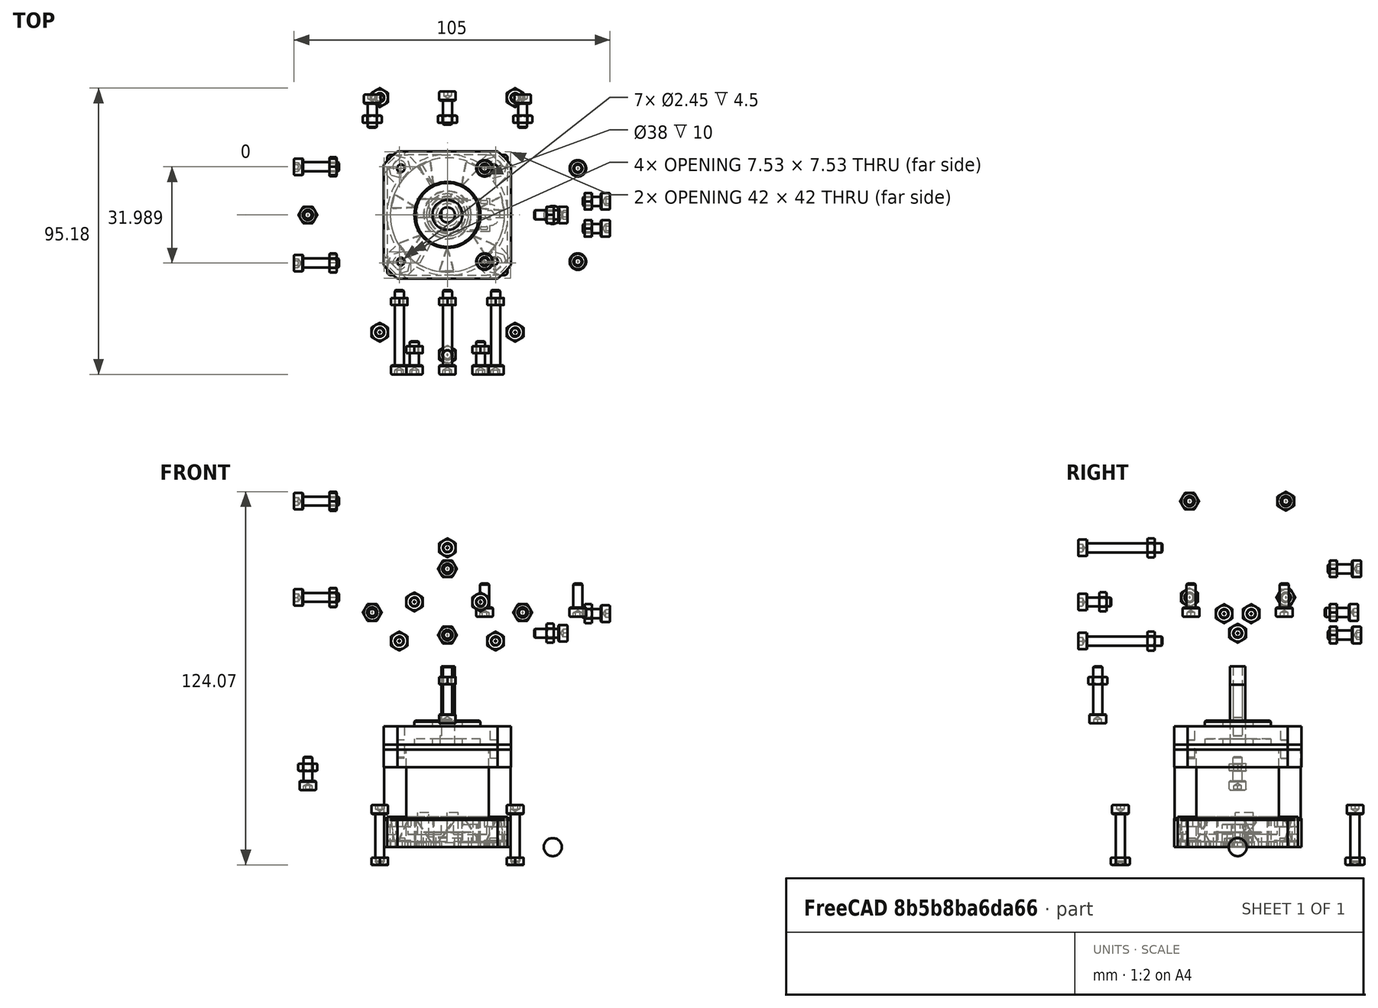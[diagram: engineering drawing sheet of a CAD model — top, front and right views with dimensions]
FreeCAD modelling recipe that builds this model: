
FCSTD DOCUMENT  (FreeCAD 0.19R24276 (Git))
Label: AssemblyArt3
License: All rights reserved
LicenseURL: http://en.wikipedia.org/wiki/All_rights_reserved
objects: Part::FeaturePython×49, App::Link×14, PartDesign::CoordinateSystem×13, App::Part×7, App::DocumentObjectGroup×6, Part::Feature×5, PartDesign::Line×5, App::FeaturePython×1, Part::Sphere×1
note: 72 computed B-rep shape members (.brp) not serialized (recipe doc carries the construction recipe, not evaluated geometry)
EXTERNAL_REF file=Art3Body.FCStd obj=LCS_Bottom
EXTERNAL_REF file=Art3Body.FCStd obj=Body002
EXTERNAL_REF file=Art23Optodisk.FCStd obj=LCS_Art23Optodisk
EXTERNAL_REF file=Art3Body.FCStd obj=LCS_OptoDisk
EXTERNAL_REF file=Art23Optodisk.FCStd obj=Body
EXTERNAL_REF file=Art3Body.FCStd obj=LCS_Pulley
EXTERNAL_REF file=Art3Pulley.FCStd obj=LCS_Art3Pulley
EXTERNAL_REF file=Art3Pulley.FCStd obj=Body
EXTERNAL_REF file=Art3Body.FCStd obj=LCS_Art4MotorHolder
EXTERNAL_REF file=Art4MotorFix.FCStd obj=LCS_Art4MotorFix
EXTERNAL_REF file=Art4MotorFix.FCStd obj=Body
EXTERNAL_REF file=Art4MotorFix.FCStd obj=LCS_Art4Motor
EXTERNAL_REF file=Art4MotorGear.FCStd obj=LCS_Art4MotorGear
EXTERNAL_REF file=Art4MotorGear.FCStd obj=Body
EXTERNAL_REF file=Art3Body.FCStd obj=LCS_Fan
EXTERNAL_REF file=Art3Body.FCStd obj=LCS_Bearing
EXTERNAL_REF file=Art3Pulley.FCStd obj=LCS_Bearing
EXTERNAL_REF file=Art3Pulley.FCStd obj=LCS_BearingFix
EXTERNAL_REF file=CommonBearingFixThrough.FCStd obj=LCS_CommonBearingFixThrough
EXTERNAL_REF file=CommonBearingFixThrough.FCStd obj=Body
EXTERNAL_REF file=Art3Body.FCStd obj=LCS_BearingFix
EXTERNAL_REF file=Art3Body.FCStd obj=LCS_OptoSensor
EXTERNAL_REF file=Art4BearingRing.FCStd obj=LCS_Art4BearingRing
EXTERNAL_REF file=Art4BearingRing.FCStd obj=Body
EXTERNAL_REF file=Art4BearingRing.FCStd obj=LCS_BallBearings
EXTERNAL_REF file=Art3Body.FCStd obj=HoleAxis_8
EXTERNAL_REF file=Art3Body.FCStd obj=HoleAxis_9
EXTERNAL_REF file=Art3Body.FCStd obj=HoleAxis_7
EXTERNAL_REF file=Art3Body.FCStd obj=HoleAxis_14
EXTERNAL_REF file=Art3Body.FCStd obj=HoleAxis_11
EXTERNAL_REF file=Art3Body.FCStd obj=HoleAxis_10
EXTERNAL_REF file=Art3Body.FCStd obj=HoleAxis_12
EXTERNAL_REF file=Art3Body.FCStd obj=HoleAxis_13
EXTERNAL_REF file=Art3Pulley.FCStd obj=HoleAxis_6
EXTERNAL_REF file=Art3Pulley.FCStd obj=HoleAxis_5
EXTERNAL_REF file=Art3Pulley.FCStd obj=HoleAxis_3
EXTERNAL_REF file=Art4MotorFix.FCStd obj=HoleAxis_2
EXTERNAL_REF file=Art4MotorFix.FCStd obj=HoleAxis_3
EXTERNAL_REF file=Art4MotorGear.FCStd obj=HoleAxis_2
EXTERNAL_REF file=Art4BearingRing.FCStd obj=HoleAxis_4
EXTERNAL_REF file=Art4BearingRing.FCStd obj=HoleAxis_3
EXTERNAL_REF file=Art4BearingRing.FCStd obj=HoleAxis_1
EXTERNAL_REF file=Art4BearingRing.FCStd obj=HoleAxis_2
EXTERNAL_REF file=CommonBearingFixThrough.FCStd obj=HoleAxis_1
EXTERNAL_REF file=CommonBearingFixThrough.FCStd obj=HoleAxis_2
EXTERNAL_REF file=Art23Optodisk.FCStd obj=HoleAxis_1
EXTERNAL_REF file=Art23Optodisk.FCStd obj=HoleAxis_2
EXTERNAL_REF file=Art3Pulley.FCStd obj=HoleAxis_1
EXTERNAL_REF file=Art3Pulley.FCStd obj=HoleAxis_4
EXTERNAL_REF file=Art3Pulley.FCStd obj=HoleAxis_2
EXTERNAL_REF file=Art3Body.FCStd obj=HoleAxis_2
EXTERNAL_REF file=Art3Body.FCStd obj=HoleAxis_1
EXTERNAL_REF file=Art3Body.FCStd obj=HoleAxis_4
EXTERNAL_REF file=Art3Body.FCStd obj=HoleAxis_3
EXTERNAL_REF file=Art3Body.FCStd obj=HoleAxis_18
EXTERNAL_REF file=Art3Body.FCStd obj=HoleAxis_17
EXTERNAL_REF file=Art3Body.FCStd obj=HoleAxis_16
EXTERNAL_REF file=Art3Body.FCStd obj=HoleAxis_15
EXTERNAL_REF file=Art4MotorFix.FCStd obj=HoleAxis_5
EXTERNAL_REF file=Art4MotorFix.FCStd obj=HoleAxis_6
EXTERNAL_REF file=Art4MotorFix.FCStd obj=HoleAxis_4
EXTERNAL_REF file=Art4MotorFix.FCStd obj=HoleAxis_1
EXTERNAL_REF file=Art3Body.FCStd obj=HoleAxis_6
EXTERNAL_REF file=Art3Body.FCStd obj=HoleAxis_5
EXTERNAL_REF file=Art4MotorGear.FCStd obj=HoleAxis_1

FEATURE [PartDesign::CoordinateSystem] LCS_Origin
  AttacherType = Attacher::AttachEngine3D
  MapMode = 2
  Support = -> [X_Axis]
FEATURE [App::DocumentObjectGroup] Constraints
FEATURE [App::FeaturePython] Variables  # WARN: FeaturePython — macro-defined, semantics opaque (R4)
FEATURE [App::Link] Art3Body_Art3Body
  AssemblyType = Asm4EE
  AttachedBy = #LCS_Art3Body
  AttachedTo = Parent Assembly#LCS_Origin
  ElementCount = 0
  LinkPlacement = pos=(-6.7e-15,2.7e-15,-7) rot=(0,0,1;0rad)
  LinkTransform = false
  Placement = pos=(-6.7e-15,2.7e-15,-7) rot=(0,0,1;0rad)
  Scale = 1
  ScaleVector = (1,1,1)
  ShowElement = true
  expr: Placement = LCS_Origin.Placement * AttachmentOffset * Art3Body#<<LCS_Art3Body>>.Placement ^ -1
FEATURE [App::Link] Art23Optodisk_Art23Optodisk
  AssemblyType = Asm4EE
  AttachedBy = #LCS_Art23Optodisk
  AttachedTo = Art3Body_Art3Body#LCS_OptoRing
  AttachmentOffset = pos=(0,0,0) rot=(0,0,1;3.14159rad)
  ElementCount = 0
  LinkPlacement = pos=(-3.27e-14,35,81.5) rot=(1,0,0;4.71239rad)
  LinkTransform = false
  Placement = pos=(-3.27e-14,35,81.5) rot=(1,0,0;4.71239rad)
  Scale = 1
  ScaleVector = (1,1,1)
  ShowElement = true
  expr: Placement = Art3Body_Art3Body.Placement * Art3Body#<<LCS_OptoRing>>.Placement * AttachmentOffset * Art23Optodisk#LCS_Art23Optodisk.Placement ^ -1
FEATURE [App::Link] Art3Pulley_Art3Pulley
  AssemblyType = Asm4EE
  AttachedBy = #LCS_Art3Pulley
  AttachedTo = Art3Body_Art3Body#LCS_Pulley
  ElementCount = 0
  LinkPlacement = pos=(-2.65e-14,-53,81.5) rot=(-1,0,0;1.5708rad)
  LinkTransform = false
  Placement = pos=(-2.65e-14,-53,81.5) rot=(-1,0,0;1.5708rad)
  Scale = 1
  ScaleVector = (1,1,1)
  ShowElement = true
  expr: Placement = Art3Body_Art3Body.Placement * Art3Body#LCS_Pulley.Placement * AttachmentOffset * Art3Pulley#LCS_Art3Pulley.Placement ^ -1
FEATURE [App::Link] Art4MotorFix_Art4MotorFix
  AssemblyType = Asm4EE
  AttachedBy = #LCS_Art4MotorFix
  AttachedTo = Art3Body_Art3Body#LCS_MotorHolder
  AttachmentOffset = pos=(0,0,0) rot=(0,-1,0;3.14159rad)
  ElementCount = 0
  LinkPlacement = pos=(27.85,-1.36e-14,82.6) rot=(0,1,0;3.14159rad)
  LinkTransform = false
  Placement = pos=(27.85,-1.36e-14,82.6) rot=(0,1,0;3.14159rad)
  Scale = 1
  ScaleVector = (1,1,1)
  ShowElement = true
  expr: Placement = Art3Body_Art3Body.Placement * Art3Body#<<LCS_MotorHolder>>.Placement * AttachmentOffset * Art4MotorFix#LCS_Art4MotorFix.Placement ^ -1
FEATURE [PartDesign::CoordinateSystem] LCS_0008
  AttacherType = Attacher::AttachEngine3D
  MapMode = 2
  Support = -> [X_Axis009]
FEATURE [Part::Feature] Part__Feature031  label="Nema-17-motor-40mm-final"
FEATURE [PartDesign::CoordinateSystem] LCS_Stepper_Nema17x40
  AttacherType = Attacher::AttachEngine3D
  MapMode = 45
  Placement = pos=(7.5e-15,0,0) rot=(0,0,1;0rad)
  Support = -> [Part__Feature031]
FEATURE [PartDesign::CoordinateSystem] LCS_Gear2  label="LCS_Gear"
  AttacherType = Attacher::AttachEngine3D
  AttachmentOffset = pos=(0,0,1.9) rot=(0,0,1;0rad)
  MapMode = 11
  Placement = pos=(0,0,44) rot=(0,0,1;1.5708rad)
  Support = -> [Part__Feature031]
FEATURE [App::Part] Stepper_Nema17x40
  Group = -> [LCS_0008,Part__Feature031,LCS_Stepper_Nema17x40,LCS_Gear2]
  Origin = -> Origin009
FEATURE [Part::Feature] Cut001
FEATURE [PartDesign::CoordinateSystem] LCS_OpticSensor
  AttacherType = Attacher::AttachEngine3D
  MapMode = 11
  Placement = pos=(14,0,0) rot=(0,0,1;1.5708rad)
  Support = -> [Cut001]
FEATURE [PartDesign::Line] HoleAxis_1
  AttacherType = Attacher::AttachEngineLine
  Length = 4.2272
  MapMode = 19
  Placement = pos=(14,0,1.5) rot=(0,0,1;0rad)
  ResizeMode = 1
  Support = -> [Cut001]
FEATURE [App::Part] Part  label="OpticSensor"
  Group = -> [Cut001,LCS_OpticSensor,HoleAxis_1]
  Origin = -> Origin010
FEATURE [Part::Feature] Chamfer_solid  label="NEMA-17_Stepper_Motor_34mm"
FEATURE [PartDesign::CoordinateSystem] LCS_Stepper_Nema17x34
  AttacherType = Attacher::AttachEngine3D
  MapMode = 45
  Placement = pos=(7.4e-15,0,34) rot=(0,0,1;0rad)
  Support = -> [Chamfer_solid]
FEATURE [PartDesign::CoordinateSystem] LCS_Gear  label="LCS_Gear001"
  AttacherType = Attacher::AttachEngine3D
  AttachmentOffset = pos=(0,0,4) rot=(0,0,1;0rad)
  MapMode = 11
  Placement = pos=(0,0,40) rot=(0,0,1;1.5708rad)
  Support = -> [Chamfer_solid]
FEATURE [App::Part] Stepper_Nema17x34
  Group = -> [Chamfer_solid,LCS_Stepper_Nema17x34,LCS_Gear]
  Origin = -> Origin011
FEATURE [App::DocumentObjectGroup] Group  label="Electronics"
  Group = -> [Stepper_Nema17x40,Part,Stepper_Nema17x34]
FEATURE [App::Link] Stepper_Nema17x34001
  AssemblyType = Asm4EE
  AttachedBy = #LCS_Stepper_Nema17x34
  AttachedTo = Art4MotorFix_Art4MotorFix#LCS_Art4Motor
  ElementCount = 0
  LinkPlacement = pos=(27.85,-1.179e-13,116.6) rot=(0,1,0;3.14159rad)
  LinkTransform = false
  Placement = pos=(27.85,-1.179e-13,116.6) rot=(0,1,0;3.14159rad)
  Scale = 1
  ScaleVector = (1,1,1)
  ShowElement = true
  expr: Placement = Art4MotorFix_Art4MotorFix.Placement * Art4MotorFix#LCS_Art4Motor.Placement * AttachmentOffset * LCS_Stepper_Nema17x34.Placement ^ -1
FEATURE [App::Link] Art4MotorGear_Art4MotorGear
  AssemblyType = Asm4EE
  AttachedBy = #LCS_Art4MotorGear
  AttachedTo = Stepper_Nema17x34001#LCS_Gear
  AttachmentOffset = pos=(0,0,0) rot=(0,1,0;3.14159rad)
  ElementCount = 0
  LinkPlacement = pos=(27.85,3.49e-14,66.6) rot=(0,-1,0;3.14159rad)
  LinkTransform = false
  Placement = pos=(27.85,3.49e-14,66.6) rot=(0,-1,0;3.14159rad)
  Scale = 1
  ScaleVector = (1,1,1)
  ShowElement = true
  expr: Placement = Stepper_Nema17x34001.Placement * LCS_Gear.Placement * AttachmentOffset * Art4MotorGear#LCS_Art4MotorGear.Placement ^ -1
FEATURE [Part::Feature] Part__Feature001  label="fan-40x40mm"
FEATURE [PartDesign::Line] HoleAxis_8
  AttacherType = Attacher::AttachEngineLine
  Length = 6.05899
  MapMode = 19
  Placement = pos=(-15.9948,15.9948,6.76) rot=(0,0,1;0rad)
  ResizeMode = 1
  Support = -> [Part__Feature001]
FEATURE [PartDesign::Line] HoleAxis_5
  AttacherType = Attacher::AttachEngineLine
  Length = 6.05899
  MapMode = 19
  Placement = pos=(15.9948,15.9948,6.76) rot=(0,0,1;4.71239rad)
  ResizeMode = 1
  Support = -> [Part__Feature001]
FEATURE [PartDesign::Line] HoleAxis_7
  AttacherType = Attacher::AttachEngineLine
  Length = 6.05899
  MapMode = 19
  Placement = pos=(-15.9948,-15.9948,6.76) rot=(0,0,1;1.5708rad)
  ResizeMode = 1
  Support = -> [Part__Feature001]
FEATURE [PartDesign::Line] HoleAxis_6
  AttacherType = Attacher::AttachEngineLine
  Length = 6.05899
  MapMode = 19
  Placement = pos=(15.9948,-15.9948,6.76) rot=(0,0,1;3.14159rad)
  ResizeMode = 1
  Support = -> [Part__Feature001]
FEATURE [PartDesign::CoordinateSystem] LCS_0001
  AttacherType = Attacher::AttachEngine3D
  MapMode = 2
  Support = -> [X_Axis002]
FEATURE [PartDesign::CoordinateSystem] LCS_Fan001
  AttacherType = Attacher::AttachEngine3D
  AttachmentOffset = pos=(0,0,-2.21) rot=(0,0,1;0rad)
  MapMode = 45
  Placement = pos=(-5e-16,5e-16,-4e-16) rot=(0,0,1;0rad)
  Support = -> [Part__Feature001]
FEATURE [App::Part] Fan_40x40
  Group = -> [LCS_0001,Part__Feature001,LCS_Fan001,HoleAxis_5,HoleAxis_6,HoleAxis_7,HoleAxis_8]
  Origin = -> Origin002
FEATURE [App::DocumentObjectGroup] Group001  label="Fans"
  Group = -> [Fan_40x40]
FEATURE [App::Link] Fan_40x40001
  AssemblyType = Asm4EE
  AttachedBy = #LCS_Fan001
  AttachedTo = Art3Body_Art3Body#LCS_Fan
  AttachmentOffset = pos=(0,0,0) rot=(0,0,1;3.14159rad)
  ElementCount = 0
  LinkPlacement = pos=(-46,1.23e-14,99) rot=(0.57735,-0.57735,0.57735;4.18879rad)
  LinkTransform = false
  Placement = pos=(-46,1.23e-14,99) rot=(0.57735,-0.57735,0.57735;4.18879rad)
  Scale = 1
  ScaleVector = (1,1,1)
  ShowElement = true
  expr: Placement = Art3Body_Art3Body.Placement * Art3Body#LCS_Fan.Placement * AttachmentOffset * LCS_Fan001.Placement ^ -1
FEATURE [Part::Feature] Compound001  label="Bearing 625ZZ"
FEATURE [PartDesign::CoordinateSystem] LCS_0
  AttacherType = Attacher::AttachEngine3D
  MapMode = 2
  Support = -> [X_Axis003]
FEATURE [App::Part] Bearing_625ZZ
  Group = -> [LCS_0,Compound001]
  Origin = -> Origin003
FEATURE [App::Link] Bearing_625ZZ001
  AssemblyType = Asm4EE
  AttachedBy = #LCS_0
  AttachedTo = Art3Body_Art3Body#LCS_Bearing
  ElementCount = 0
  LinkPlacement = pos=(-3.9e-15,32,81.5) rot=(0.57735,0.57735,0.57735;4.18879rad)
  LinkTransform = false
  Placement = pos=(-3.9e-15,32,81.5) rot=(0.57735,0.57735,0.57735;4.18879rad)
  Scale = 1
  ScaleVector = (1,1,1)
  ShowElement = true
  expr: Placement = Art3Body_Art3Body.Placement * Art3Body#LCS_Bearing.Placement * AttachmentOffset * LCS_0.Placement ^ -1
FEATURE [App::Link] Bearing_625ZZ002
  AssemblyType = Asm4EE
  AttachedBy = #LCS_0
  AttachedTo = Art3Pulley_Art3Pulley#LCS_Bearing
  AttachmentOffset = pos=(0,0,0) rot=(0,1,0;3.14159rad)
  ElementCount = 0
  LinkPlacement = pos=(-2.5e-14,-44,81.5) rot=(0.57735,0.57735,-0.57735;2.0944rad)
  LinkTransform = false
  Placement = pos=(-2.5e-14,-44,81.5) rot=(0.57735,0.57735,-0.57735;2.0944rad)
  Scale = 1
  ScaleVector = (1,1,1)
  ShowElement = true
  expr: Placement = Art3Pulley_Art3Pulley.Placement * Art3Pulley#LCS_Bearing.Placement * AttachmentOffset * LCS_0.Placement ^ -1
FEATURE [App::Link] CommonBearingFixThrough_CommonBearingFixThrough
  AssemblyType = Asm4EE
  AttachedBy = #LCS_CommonBearingFixThrough
  AttachedTo = Art3Pulley_Art3Pulley#LCS_BearingFix
  AttachmentOffset = pos=(0,0,0) rot=(0,1,0;3.14159rad)
  ElementCount = 0
  LinkPlacement = pos=(-2.62e-14,-49,81.5) rot=(-1,0,0;4.71239rad)
  LinkTransform = false
  Placement = pos=(-2.62e-14,-49,81.5) rot=(-1,0,0;4.71239rad)
  Scale = 1
  ScaleVector = (1,1,1)
  ShowElement = true
  expr: Placement = Art3Pulley_Art3Pulley.Placement * Art3Pulley#LCS_BearingFix.Placement * AttachmentOffset * CommonBearingFixThrough#LCS_CommonBearingFixThrough.Placement ^ -1
FEATURE [App::Link] CommonBearingFixThrough_CommonBearingFixThrough001
  AssemblyType = Asm4EE
  AttachedBy = #LCS_CommonBearingFixThrough
  AttachedTo = Art3Body_Art3Body#LCS_BearingFix
  ElementCount = 0
  LinkPlacement = pos=(-1.61e-14,37,81.5) rot=(-0.57735,-0.57735,-0.57735;2.0944rad)
  LinkTransform = false
  Placement = pos=(-1.61e-14,37,81.5) rot=(-0.57735,-0.57735,-0.57735;2.0944rad)
  Scale = 1
  ScaleVector = (1,1,1)
  ShowElement = true
  expr: Placement = Art3Body_Art3Body.Placement * Art3Body#LCS_BearingFix.Placement * AttachmentOffset * CommonBearingFixThrough#LCS_CommonBearingFixThrough.Placement ^ -1
FEATURE [App::Link] OpticSensor  label="OpticSensor001"
  AssemblyType = Asm4EE
  AttachedBy = #LCS_OpticSensor
  AttachedTo = Art3Body_Art3Body#LCS_OptoSensor
  AttachmentOffset = pos=(0,0,0) rot=(0,0,1;3.14159rad)
  ElementCount = 0
  LinkPlacement = pos=(-32.4,-1e-16,23.5) rot=(0,-1,0;3.14159rad)
  LinkTransform = false
  Placement = pos=(-32.4,-1e-16,23.5) rot=(0,-1,0;3.14159rad)
  Scale = 1
  ScaleVector = (1,1,1)
  ShowElement = true
  expr: Placement = Art3Body_Art3Body.Placement * Art3Body#LCS_OptoSensor.Placement * AttachmentOffset * LCS_OpticSensor.Placement ^ -1
FEATURE [App::Link] Art4BearingRing_Art4BearingRing
  AssemblyType = Asm4EE
  AttachedBy = #LCS_Art4BearingRing
  AttachedTo = Art3Body_Art3Body#LCS_Bottom
  AttachmentOffset = pos=(0,0,4) rot=(0.707107,-0.707107,0;3.14159rad)
  ElementCount = 0
  LinkPlacement = pos=(-5e-16,0,4) rot=(0.707107,-0.707107,0;3.14159rad)
  LinkTransform = false
  Placement = pos=(-5e-16,0,4) rot=(0.707107,-0.707107,0;3.14159rad)
  Scale = 1
  ScaleVector = (1,1,1)
  ShowElement = true
  expr: Placement = Art3Body_Art3Body.Placement * Art3Body#LCS_Bottom.Placement * AttachmentOffset * Art4BearingRing#LCS_Art4BearingRing.Placement ^ -1
FEATURE [Part::Sphere] Sphere
  Angle1 = -90
  Angle2 = 90
  Angle3 = 360
  AttacherType = Attacher::AttachEngine3D
  MapMode = 0
  Placement = pos=(35,0,0) rot=(0,0,1;0rad)
  Radius = 3
FEATURE [Part::FeaturePython] Array  # WARN: FeaturePython — macro-defined, semantics opaque (R4)
  Angle = 360
  ArrayType = 1
  Axis = (0,0,1)
  Base = -> Sphere
  Center = (0,0,0)
  Count = 36
  ExpandArray = false
  Fuse = false
  IntervalAxis = (0,0,0)
  IntervalX = (50,0,0)
  IntervalY = (0,50,0)
  IntervalZ = (0,0,50)
  LinkTransform = false
  NumberCircles = 3
  NumberPolar = 36
  NumberX = 2
  NumberY = 2
  NumberZ = 1
  RadialDistance = 50
  Scale = 1
  ScaleVector = (1,1,1)
  Symmetry = 1
  TangentialDistance = 25
FEATURE [PartDesign::CoordinateSystem] LCS_BearingBalls
  AttacherType = Attacher::AttachEngine3D
  MapMode = 0
FEATURE [App::Part] Part001  label="BearingBalls"
  Group = -> [Sphere,Array,LCS_BearingBalls]
  Origin = -> Origin012
FEATURE [App::DocumentObjectGroup] Group002  label="Bearing"
  Group = -> [Bearing_625ZZ,Part001]
FEATURE [App::DocumentObjectGroup] Parts
  Group = -> [Group,Group001,Group002]
FEATURE [App::Link] BearingBalls  label="BearingBalls001"
  AssemblyType = Asm4EE
  AttachedBy = #LCS_BearingBalls
  AttachedTo = Art4BearingRing_Art4BearingRing#LCS_BallBearings
  AttachmentOffset = pos=(0,0,1) rot=(0,0,1;0rad)
  ElementCount = 0
  LinkPlacement = pos=(-3e-16,-7e-16,-1) rot=(0.707107,-0.707107,0;3.14159rad)
  LinkTransform = false
  Placement = pos=(-3e-16,-7e-16,-1) rot=(0.707107,-0.707107,0;3.14159rad)
  Scale = 1
  ScaleVector = (1,1,1)
  ShowElement = true
  expr: Placement = Art4BearingRing_Art4BearingRing.Placement * Art4BearingRing#LCS_BallBearings.Placement * AttachmentOffset * LCS_BearingBalls.Placement ^ -1
FEATURE [Part::FeaturePython] Nut  label="M3-Nut"  # WARN: FeaturePython — macro-defined, semantics opaque (R4)
  AssemblyType = Asm4EE
  AttachedBy = Origin
  AttachedTo = Art3Body_Art3Body#HoleAxis_8
  AttachmentOffset = pos=(0,0,0) rot=(0,0,1;1.5708rad)
  Placement = pos=(-16,-30,68.5) rot=(0.57735,0.57735,0.57735;4.18879rad)
  diameter = 4
  invert = false
  matchOuter = false
  offset = 0
  thread = false
  type = 7
  expr: Placement = Art3Body_Art3Body.Placement * Art3Body#HoleAxis_8.Placement * AttachmentOffset
FEATURE [Part::FeaturePython] Nut001  label="M3-Nut022"  # WARN: FeaturePython — macro-defined, semantics opaque (R4)
  AssemblyType = Asm4EE
  AttachedBy = Origin
  AttachedTo = Art3Body_Art3Body#HoleAxis_9
  AttachmentOffset = pos=(0,0,0) rot=(0,0,1;1.5708rad)
  Placement = pos=(-1.2e-14,-30,99.5) rot=(0.57735,0.57735,0.57735;4.18879rad)
  diameter = 4
  invert = false
  matchOuter = false
  offset = 0
  thread = false
  type = 7
  expr: Placement = Art3Body_Art3Body.Placement * Art3Body#HoleAxis_9.Placement * AttachmentOffset
FEATURE [Part::FeaturePython] Nut002  label="M3-Nut023"  # WARN: FeaturePython — macro-defined, semantics opaque (R4)
  AssemblyType = Asm4EE
  AttachedBy = Origin
  AttachedTo = Art3Body_Art3Body#HoleAxis_7
  AttachmentOffset = pos=(0,0,0) rot=(0,0,1;1.5708rad)
  Placement = pos=(16,-30,68.5) rot=(0.57735,0.57735,0.57735;4.18879rad)
  diameter = 4
  invert = false
  matchOuter = false
  offset = 0
  thread = false
  type = 7
  expr: Placement = Art3Body_Art3Body.Placement * Art3Body#HoleAxis_7.Placement * AttachmentOffset
FEATURE [Part::FeaturePython] Nut003  label="M3-Nut024"  # WARN: FeaturePython — macro-defined, semantics opaque (R4)
  AssemblyType = Asm4EE
  AttachedBy = Origin
  AttachedTo = Art3Body_Art3Body#HoleAxis_14
  AttachmentOffset = pos=(0,0,0) rot=(1,0,0;3.14159rad)
  Placement = pos=(-46.4,-3e-15,25.35) rot=(0,0,1;0rad)
  diameter = 4
  invert = false
  matchOuter = false
  offset = 0
  thread = false
  type = 7
  expr: Placement = Art3Body_Art3Body.Placement * Art3Body#HoleAxis_14.Placement * AttachmentOffset
FEATURE [Part::FeaturePython] Nut004  label="M3-Nut025"  # WARN: FeaturePython — macro-defined, semantics opaque (R4)
  AssemblyType = Asm4EE
  AttachedBy = Origin
  AttachedTo = Art3Body_Art3Body#HoleAxis_11
  AttachmentOffset = pos=(0,0,0) rot=(-1,0,0;3.14159rad)
  Placement = pos=(25,33,78) rot=(0,0.707107,-0.707107;3.14159rad)
  diameter = 4
  invert = false
  matchOuter = false
  offset = 0
  thread = false
  type = 7
  expr: Placement = Art3Body_Art3Body.Placement * Art3Body#HoleAxis_11.Placement * AttachmentOffset
FEATURE [Part::FeaturePython] Nut005  label="M3-Nut026"  # WARN: FeaturePython — macro-defined, semantics opaque (R4)
  AssemblyType = Asm4EE
  AttachedBy = Origin
  AttachedTo = Art3Body_Art3Body#HoleAxis_10
  AttachmentOffset = pos=(0,0,0) rot=(1,0,0;3.14159rad)
  Placement = pos=(-8e-15,33,70.5) rot=(0,0.707107,-0.707107;3.14159rad)
  diameter = 4
  invert = false
  matchOuter = false
  offset = 0
  thread = false
  type = 7
  expr: Placement = Art3Body_Art3Body.Placement * Art3Body#HoleAxis_10.Placement * AttachmentOffset
FEATURE [Part::FeaturePython] Nut006  label="M3-Nut027"  # WARN: FeaturePython — macro-defined, semantics opaque (R4)
  AssemblyType = Asm4EE
  AttachedBy = Origin
  AttachedTo = Art3Body_Art3Body#HoleAxis_12
  AttachmentOffset = pos=(0,0,0) rot=(1,0,0;3.14159rad)
  Placement = pos=(-25,33,78) rot=(0,0.707107,-0.707107;3.14159rad)
  diameter = 4
  invert = false
  matchOuter = false
  offset = 0
  thread = false
  type = 7
  expr: Placement = Art3Body_Art3Body.Placement * Art3Body#HoleAxis_12.Placement * AttachmentOffset
FEATURE [Part::FeaturePython] Nut007  label="M3-Nut028"  # WARN: FeaturePython — macro-defined, semantics opaque (R4)
  AssemblyType = Asm4EE
  AttachedBy = Origin
  AttachedTo = Art3Body_Art3Body#HoleAxis_13
  AttachmentOffset = pos=(0,0,0) rot=(1,0,0;3.14159rad)
  Placement = pos=(-9e-15,33,92.5) rot=(0,0.707107,-0.707107;3.14159rad)
  diameter = 4
  invert = false
  matchOuter = false
  offset = 0
  thread = false
  type = 7
  expr: Placement = Art3Body_Art3Body.Placement * Art3Body#HoleAxis_13.Placement * AttachmentOffset
FEATURE [Part::FeaturePython] Nut008  label="M3-Nut029"  # WARN: FeaturePython — macro-defined, semantics opaque (R4)
  AssemblyType = Asm4EE
  AttachedBy = Origin
  AttachedTo = Art3Pulley_Art3Pulley#HoleAxis_6
  AttachmentOffset = pos=(0,0,0) rot=(0.707107,-0.707107,0;3.14159rad)
  Placement = pos=(-11,-46,81.5) rot=(0.57735,-0.57735,-0.57735;4.18879rad)
  diameter = 4
  invert = false
  matchOuter = false
  offset = 0
  thread = false
  type = 7
  expr: Placement = Art3Pulley_Art3Pulley.Placement * Art3Pulley#HoleAxis_6.Placement * AttachmentOffset
FEATURE [Part::FeaturePython] Nut009  label="M3-Nut030"  # WARN: FeaturePython — macro-defined, semantics opaque (R4)
  AssemblyType = Asm4EE
  AttachedBy = Origin
  AttachedTo = Art3Pulley_Art3Pulley#HoleAxis_5
  AttachmentOffset = pos=(0,0,0) rot=(0.707107,0.707107,0;3.14159rad)
  Placement = pos=(11,-46,81.5) rot=(0.57735,0.57735,0.57735;4.18879rad)
  diameter = 4
  invert = false
  matchOuter = false
  offset = 0
  thread = false
  type = 7
  expr: Placement = Art3Pulley_Art3Pulley.Placement * Art3Pulley#HoleAxis_5.Placement * AttachmentOffset
FEATURE [Part::FeaturePython] Nut010  label="M3-Nut031"  # WARN: FeaturePython — macro-defined, semantics opaque (R4)
  AssemblyType = Asm4EE
  AttachedBy = Origin
  AttachedTo = Art3Pulley_Art3Pulley#HoleAxis_3
  AttachmentOffset = pos=(0,0,0) rot=(0.707107,-0.707107,0;3.14159rad)
  Placement = pos=(-2.2e-14,-46.5,54.15) rot=(0,0,1;1.5708rad)
  diameter = 4
  invert = false
  matchOuter = false
  offset = 0
  thread = false
  type = 7
  expr: Placement = Art3Pulley_Art3Pulley.Placement * Art3Pulley#HoleAxis_3.Placement * AttachmentOffset
FEATURE [Part::FeaturePython] Nut011  label="M3-Nut032"  # WARN: FeaturePython — macro-defined, semantics opaque (R4)
  AssemblyType = Asm4EE
  AttachedBy = Origin
  AttachedTo = Art4MotorFix_Art4MotorFix#HoleAxis_2
  AttachmentOffset = pos=(0,0,0) rot=(0.707107,-0.707107,0;3.14159rad)
  Placement = pos=(48,-4.5,77.6) rot=(0,-1,0;1.5708rad)
  diameter = 4
  invert = false
  matchOuter = false
  offset = 0
  thread = false
  type = 7
  expr: Placement = Art4MotorFix_Art4MotorFix.Placement * Art4MotorFix#HoleAxis_2.Placement * AttachmentOffset
FEATURE [Part::FeaturePython] Nut012  label="M3-Nut033"  # WARN: FeaturePython — macro-defined, semantics opaque (R4)
  AssemblyType = Asm4EE
  AttachedBy = Origin
  AttachedTo = Art4MotorFix_Art4MotorFix#HoleAxis_3
  AttachmentOffset = pos=(0,0,0) rot=(0.707107,-0.707107,0;3.14159rad)
  Placement = pos=(48,4.5,77.6) rot=(0,-1,0;1.5708rad)
  diameter = 4
  invert = false
  matchOuter = false
  offset = 0
  thread = false
  type = 7
  expr: Placement = Art4MotorFix_Art4MotorFix.Placement * Art4MotorFix#HoleAxis_3.Placement * AttachmentOffset
FEATURE [Part::FeaturePython] Nut013  label="M3-Nut050"  # WARN: FeaturePython — macro-defined, semantics opaque (R4)
  AssemblyType = Asm4EE
  AttachedBy = Origin
  AttachedTo = Art4MotorGear_Art4MotorGear#HoleAxis_2
  AttachmentOffset = pos=(0,0,0) rot=(0,0,1;1.5708rad)
  Placement = pos=(35.35,2.6e-14,71.1) rot=(0.707107,0,-0.707107;3.14159rad)
  diameter = 4
  invert = false
  matchOuter = false
  offset = 0
  thread = false
  type = 7
  expr: Placement = Art4MotorGear_Art4MotorGear.Placement * Art4MotorGear#HoleAxis_2.Placement * AttachmentOffset
FEATURE [Part::FeaturePython] Nut014  label="M3-Nut035"  # WARN: FeaturePython — macro-defined, semantics opaque (R4)
  AssemblyType = Asm4EE
  AttachedBy = Origin
  AttachedTo = Art4BearingRing_Art4BearingRing#HoleAxis_4
  Placement = pos=(22.5,-39,-3.5) rot=(0.707107,0.707107,0;3.14159rad)
  diameter = 4
  invert = false
  matchOuter = false
  offset = 0
  thread = false
  type = 7
  expr: Placement = Art4BearingRing_Art4BearingRing.Placement * Art4BearingRing#HoleAxis_4.Placement * AttachmentOffset
FEATURE [Part::FeaturePython] Nut015  label="M3-Nut036"  # WARN: FeaturePython — macro-defined, semantics opaque (R4)
  AssemblyType = Asm4EE
  AttachedBy = Origin
  AttachedTo = Art4BearingRing_Art4BearingRing#HoleAxis_3
  Placement = pos=(22.5,39,-3.5) rot=(0.707107,0.707107,0;3.14159rad)
  diameter = 4
  invert = false
  matchOuter = false
  offset = 0
  thread = false
  type = 7
  expr: Placement = Art4BearingRing_Art4BearingRing.Placement * Art4BearingRing#HoleAxis_3.Placement * AttachmentOffset
FEATURE [Part::FeaturePython] Nut016  label="M3-Nut037"  # WARN: FeaturePython — macro-defined, semantics opaque (R4)
  AssemblyType = Asm4EE
  AttachedBy = Origin
  AttachedTo = Art4BearingRing_Art4BearingRing#HoleAxis_1
  Placement = pos=(-22.5,-39,-3.5) rot=(0.707107,0.707107,0;3.14159rad)
  diameter = 4
  invert = false
  matchOuter = false
  offset = 0
  thread = false
  type = 7
  expr: Placement = Art4BearingRing_Art4BearingRing.Placement * Art4BearingRing#HoleAxis_1.Placement * AttachmentOffset
FEATURE [Part::FeaturePython] Nut017  label="M3-Nut038"  # WARN: FeaturePython — macro-defined, semantics opaque (R4)
  AssemblyType = Asm4EE
  AttachedBy = Origin
  AttachedTo = Art4BearingRing_Art4BearingRing#HoleAxis_2
  Placement = pos=(-22.5,39,-3.5) rot=(0.707107,0.707107,0;3.14159rad)
  diameter = 4
  invert = false
  matchOuter = false
  offset = 0
  thread = false
  type = 7
  expr: Placement = Art4BearingRing_Art4BearingRing.Placement * Art4BearingRing#HoleAxis_2.Placement * AttachmentOffset
FEATURE [Part::FeaturePython] Nut018  label="M3-Nut051"  # WARN: FeaturePython — macro-defined, semantics opaque (R4)
  AssemblyType = Asm4EE
  AttachedBy = Origin
  AttachedTo = Fan_40x40001#HoleAxis_7
  AttachmentOffset = pos=(0,0,0) rot=(0,0,-1;3.14159rad)
  Placement = pos=(-39.24,15.9948,114.995) rot=(0.707107,0,0.707107;3.14159rad)
  diameter = 4
  invert = false
  matchOuter = false
  offset = 0
  thread = false
  type = 7
  expr: Placement = Fan_40x40001.Placement * HoleAxis_7.Placement * AttachmentOffset
FEATURE [Part::FeaturePython] Nut019  label="M3-Nut048"  # WARN: FeaturePython — macro-defined, semantics opaque (R4)
  AssemblyType = Asm4EE
  AttachedBy = Origin
  AttachedTo = Fan_40x40001#HoleAxis_8
  Placement = pos=(-39.24,15.9948,83.0052) rot=(0.57735,-0.57735,0.57735;4.18879rad)
  diameter = 4
  invert = false
  matchOuter = false
  offset = 0
  thread = false
  type = 7
  expr: Placement = Fan_40x40001.Placement * HoleAxis_8.Placement * AttachmentOffset
FEATURE [Part::FeaturePython] Nut020  label="M3-Nut052"  # WARN: FeaturePython — macro-defined, semantics opaque (R4)
  AssemblyType = Asm4EE
  AttachedBy = Origin
  AttachedTo = Fan_40x40001#HoleAxis_6
  Placement = pos=(-39.24,-15.9948,114.995) rot=(0.57735,0.57735,0.57735;2.0944rad)
  diameter = 4
  invert = false
  matchOuter = false
  offset = 0
  thread = false
  type = 7
  expr: Placement = Fan_40x40001.Placement * HoleAxis_6.Placement * AttachmentOffset
FEATURE [Part::FeaturePython] Nut021  label="M3-Nut049"  # WARN: FeaturePython — macro-defined, semantics opaque (R4)
  AssemblyType = Asm4EE
  AttachedBy = Origin
  AttachedTo = Fan_40x40001#HoleAxis_5
  Placement = pos=(-39.24,-15.9948,83.0052) rot=(0.707107,0,0.707107;3.14159rad)
  diameter = 4
  invert = false
  matchOuter = false
  offset = 0
  thread = false
  type = 7
  expr: Placement = Fan_40x40001.Placement * HoleAxis_5.Placement * AttachmentOffset
FEATURE [Part::FeaturePython] Screw  label="M3x8-Screw"  # WARN: FeaturePython — macro-defined, semantics opaque (R4)
  AssemblyType = Asm4EE
  AttachedBy = Origin
  AttachedTo = OpticSensor#HoleAxis_1
  Placement = pos=(-46.4,-3e-15,22) rot=(0,1,0;3.14159rad)
  diameter = 4
  invert = false
  length = 2
  lengthCustom = 8
  matchOuter = false
  offset = 0
  thread = false
  type = 33
  expr: Placement = OpticSensor.Placement * HoleAxis_1.Placement * AttachmentOffset
FEATURE [Part::FeaturePython] Screw001  label="M3x8-Screw005"  # WARN: FeaturePython — macro-defined, semantics opaque (R4)
  AssemblyType = Asm4EE
  AttachedBy = Origin
  AttachedTo = CommonBearingFixThrough_CommonBearingFixThrough001#HoleAxis_1
  AttachmentOffset = pos=(0,0,0) rot=(1,0,0;3.14159rad)
  Placement = pos=(-1.6e-14,38,70.5) rot=(-0.57735,-0.57735,-0.57735;2.0944rad)
  diameter = 4
  invert = false
  length = 2
  lengthCustom = 8
  matchOuter = false
  offset = 0
  thread = false
  type = 33
  expr: Placement = CommonBearingFixThrough_CommonBearingFixThrough001.Placement * CommonBearingFixThrough#HoleAxis_1.Placement * AttachmentOffset
FEATURE [Part::FeaturePython] Screw002  label="M3x8-Screw006"  # WARN: FeaturePython — macro-defined, semantics opaque (R4)
  AssemblyType = Asm4EE
  AttachedBy = Origin
  AttachedTo = CommonBearingFixThrough_CommonBearingFixThrough001#HoleAxis_2
  AttachmentOffset = pos=(0,0,0) rot=(-1,0,0;3.14159rad)
  Placement = pos=(-1.6e-14,38,92.5) rot=(-0.57735,-0.57735,-0.57735;2.0944rad)
  diameter = 4
  invert = false
  length = 2
  lengthCustom = 8
  matchOuter = false
  offset = 0
  thread = false
  type = 33
  expr: Placement = CommonBearingFixThrough_CommonBearingFixThrough001.Placement * CommonBearingFixThrough#HoleAxis_2.Placement * AttachmentOffset
FEATURE [Part::FeaturePython] Screw003  label="M3x8-Screw007"  # WARN: FeaturePython — macro-defined, semantics opaque (R4)
  AssemblyType = Asm4EE
  AttachedBy = Origin
  AttachedTo = Art23Optodisk_Art23Optodisk#HoleAxis_1
  AttachmentOffset = pos=(0,0,0) rot=(1,0,0;3.14159rad)
  Placement = pos=(-25,37,78) rot=(-1,0,0;1.5708rad)
  diameter = 4
  invert = false
  length = 2
  lengthCustom = 8
  matchOuter = false
  offset = 0
  thread = false
  type = 33
  expr: Placement = Art23Optodisk_Art23Optodisk.Placement * Art23Optodisk#HoleAxis_1.Placement * AttachmentOffset
FEATURE [Part::FeaturePython] Screw004  label="M3x8-Screw008"  # WARN: FeaturePython — macro-defined, semantics opaque (R4)
  AssemblyType = Asm4EE
  AttachedBy = Origin
  AttachedTo = Art23Optodisk_Art23Optodisk#HoleAxis_2
  AttachmentOffset = pos=(0,0,0) rot=(1,0,0;3.14159rad)
  Placement = pos=(25,37,78) rot=(-1,0,0;1.5708rad)
  diameter = 4
  invert = false
  length = 2
  lengthCustom = 8
  matchOuter = false
  offset = 0
  thread = false
  type = 33
  expr: Placement = Art23Optodisk_Art23Optodisk.Placement * Art23Optodisk#HoleAxis_2.Placement * AttachmentOffset
FEATURE [Part::FeaturePython] Screw005  label="M3x8-Screw011"  # WARN: FeaturePython — macro-defined, semantics opaque (R4)
  AssemblyType = Asm4EE
  AttachedBy = Origin
  AttachedTo = CommonBearingFixThrough_CommonBearingFixThrough#HoleAxis_2
  AttachmentOffset = pos=(0,0,0) rot=(1,0,0;3.14159rad)
  Placement = pos=(11,-50,81.5) rot=(1,0,0;1.5708rad)
  diameter = 4
  invert = false
  length = 2
  lengthCustom = 8
  matchOuter = false
  offset = 0
  thread = false
  type = 33
  expr: Placement = CommonBearingFixThrough_CommonBearingFixThrough.Placement * CommonBearingFixThrough#HoleAxis_2.Placement * AttachmentOffset
FEATURE [Part::FeaturePython] Screw006  label="M3x8-Screw012"  # WARN: FeaturePython — macro-defined, semantics opaque (R4)
  AssemblyType = Asm4EE
  AttachedBy = Origin
  AttachedTo = CommonBearingFixThrough_CommonBearingFixThrough#HoleAxis_1
  AttachmentOffset = pos=(0,0,0) rot=(1,0,0;3.14159rad)
  Placement = pos=(-11,-50,81.5) rot=(1,0,0;1.5708rad)
  diameter = 4
  invert = false
  length = 2
  lengthCustom = 8
  matchOuter = false
  offset = 0
  thread = false
  type = 33
  expr: Placement = CommonBearingFixThrough_CommonBearingFixThrough.Placement * CommonBearingFixThrough#HoleAxis_1.Placement * AttachmentOffset
FEATURE [Part::FeaturePython] Screw007  label="M3x25-Screw"  # WARN: FeaturePython — macro-defined, semantics opaque (R4)
  AssemblyType = Asm4EE
  AttachedBy = Origin
  AttachedTo = Art3Pulley_Art3Pulley#HoleAxis_1
  Placement = pos=(16,-50,68.5) rot=(1,0,0;1.5708rad)
  diameter = 4
  invert = false
  length = 8
  lengthCustom = 25
  matchOuter = false
  offset = 0
  thread = false
  type = 33
  expr: Placement = Art3Pulley_Art3Pulley.Placement * Art3Pulley#HoleAxis_1.Placement * AttachmentOffset
FEATURE [Part::FeaturePython] Screw008  label="M3x25-Screw003"  # WARN: FeaturePython — macro-defined, semantics opaque (R4)
  AssemblyType = Asm4EE
  AttachedBy = Origin
  AttachedTo = Art3Pulley_Art3Pulley#HoleAxis_4
  Placement = pos=(-2.9e-14,-50,99.5) rot=(1,0,0;1.5708rad)
  diameter = 4
  invert = false
  length = 8
  lengthCustom = 25
  matchOuter = false
  offset = 0
  thread = false
  type = 33
  expr: Placement = Art3Pulley_Art3Pulley.Placement * Art3Pulley#HoleAxis_4.Placement * AttachmentOffset
FEATURE [Part::FeaturePython] Screw009  label="M3x25-Screw004"  # WARN: FeaturePython — macro-defined, semantics opaque (R4)
  AssemblyType = Asm4EE
  AttachedBy = Origin
  AttachedTo = Art3Pulley_Art3Pulley#HoleAxis_2
  Placement = pos=(-16,-50,68.5) rot=(1,0,0;1.5708rad)
  diameter = 4
  invert = false
  length = 8
  lengthCustom = 25
  matchOuter = false
  offset = 0
  thread = false
  type = 33
  expr: Placement = Art3Pulley_Art3Pulley.Placement * Art3Pulley#HoleAxis_2.Placement * AttachmentOffset
FEATURE [Part::FeaturePython] Screw010  label="M3x16-Screw"  # WARN: FeaturePython — macro-defined, semantics opaque (R4)
  AssemblyType = Asm4EE
  AttachedBy = Origin
  AttachedTo = Art3Pulley_Art3Pulley#HoleAxis_3
  AttachmentOffset = pos=(0,0,10) rot=(0,0,1;0rad)
  Placement = pos=(-2.1e-14,-46.5,44.15) rot=(1,0,0;3.14159rad)
  diameter = 4
  invert = false
  length = 6
  lengthCustom = 16
  matchOuter = false
  offset = 0
  thread = false
  type = 33
  expr: Placement = Art3Pulley_Art3Pulley.Placement * Art3Pulley#HoleAxis_3.Placement * AttachmentOffset
FEATURE [Part::FeaturePython] Screw011  label="M3x12-Screw"  # WARN: FeaturePython — macro-defined, semantics opaque (R4)
  AssemblyType = Asm4EE
  AttachedBy = Origin
  AttachedTo = Art3Body_Art3Body#HoleAxis_2
  AttachmentOffset = pos=(0,0,0) rot=(1,0,0;3.14159rad)
  Placement = pos=(-48,-16,83) rot=(0.57735,0.57735,-0.57735;4.18879rad)
  diameter = 4
  invert = false
  length = 4
  lengthCustom = 12
  matchOuter = false
  offset = 0
  thread = false
  type = 33
  expr: Placement = Art3Body_Art3Body.Placement * Art3Body#HoleAxis_2.Placement * AttachmentOffset
FEATURE [Part::FeaturePython] Screw012  label="M3x12-Screw004"  # WARN: FeaturePython — macro-defined, semantics opaque (R4)
  AssemblyType = Asm4EE
  AttachedBy = Origin
  AttachedTo = Art3Body_Art3Body#HoleAxis_1
  AttachmentOffset = pos=(0,0,0) rot=(1,0,0;3.14159rad)
  Placement = pos=(-48,-16,115) rot=(0.57735,0.57735,-0.57735;4.18879rad)
  diameter = 4
  invert = false
  length = 4
  lengthCustom = 12
  matchOuter = false
  offset = 0
  thread = false
  type = 33
  expr: Placement = Art3Body_Art3Body.Placement * Art3Body#HoleAxis_1.Placement * AttachmentOffset
FEATURE [Part::FeaturePython] Screw013  label="M3x12-Screw005"  # WARN: FeaturePython — macro-defined, semantics opaque (R4)
  AssemblyType = Asm4EE
  AttachedBy = Origin
  AttachedTo = Art3Body_Art3Body#HoleAxis_4
  AttachmentOffset = pos=(0,0,0) rot=(1,0,0;3.14159rad)
  Placement = pos=(-48,16,83) rot=(0.57735,0.57735,-0.57735;4.18879rad)
  diameter = 4
  invert = false
  length = 4
  lengthCustom = 12
  matchOuter = false
  offset = 0
  thread = false
  type = 33
  expr: Placement = Art3Body_Art3Body.Placement * Art3Body#HoleAxis_4.Placement * AttachmentOffset
FEATURE [Part::FeaturePython] Screw014  label="M3x12-Screw006"  # WARN: FeaturePython — macro-defined, semantics opaque (R4)
  AssemblyType = Asm4EE
  AttachedBy = Origin
  AttachedTo = Art3Body_Art3Body#HoleAxis_3
  AttachmentOffset = pos=(0,0,0) rot=(1,0,0;3.14159rad)
  Placement = pos=(-48,16,115) rot=(0.57735,0.57735,-0.57735;4.18879rad)
  diameter = 4
  invert = false
  length = 4
  lengthCustom = 12
  matchOuter = false
  offset = 0
  thread = false
  type = 33
  expr: Placement = Art3Body_Art3Body.Placement * Art3Body#HoleAxis_3.Placement * AttachmentOffset
FEATURE [Part::FeaturePython] Screw015  label="M3x16-Screw005"  # WARN: FeaturePython — macro-defined, semantics opaque (R4)
  AssemblyType = Asm4EE
  AttachedBy = Origin
  AttachedTo = Art3Body_Art3Body#HoleAxis_18
  AttachmentOffset = pos=(0,0,0) rot=(1,0,0;3.14159rad)
  Placement = pos=(-22.5,-39,11) rot=(0,0,1;0rad)
  diameter = 4
  invert = false
  length = 6
  lengthCustom = 16
  matchOuter = false
  offset = 0
  thread = false
  type = 33
  expr: Placement = Art3Body_Art3Body.Placement * Art3Body#HoleAxis_18.Placement * AttachmentOffset
FEATURE [Part::FeaturePython] Screw016  label="M3x16-Screw006"  # WARN: FeaturePython — macro-defined, semantics opaque (R4)
  AssemblyType = Asm4EE
  AttachedBy = Origin
  AttachedTo = Art3Body_Art3Body#HoleAxis_17
  AttachmentOffset = pos=(0,0,0) rot=(1,0,0;3.14159rad)
  Placement = pos=(22.5,-39,11) rot=(0,0,1;0rad)
  diameter = 4
  invert = false
  length = 6
  lengthCustom = 16
  matchOuter = false
  offset = 0
  thread = false
  type = 33
  expr: Placement = Art3Body_Art3Body.Placement * Art3Body#HoleAxis_17.Placement * AttachmentOffset
FEATURE [Part::FeaturePython] Screw017  label="M3x16-Screw007"  # WARN: FeaturePython — macro-defined, semantics opaque (R4)
  AssemblyType = Asm4EE
  AttachedBy = Origin
  AttachedTo = Art3Body_Art3Body#HoleAxis_16
  AttachmentOffset = pos=(0,0,0) rot=(1,0,0;3.14159rad)
  Placement = pos=(-22.5,39,11) rot=(0,0,1;0rad)
  diameter = 4
  invert = false
  length = 6
  lengthCustom = 16
  matchOuter = false
  offset = 0
  thread = false
  type = 33
  expr: Placement = Art3Body_Art3Body.Placement * Art3Body#HoleAxis_16.Placement * AttachmentOffset
FEATURE [Part::FeaturePython] Screw018  label="M3x16-Screw008"  # WARN: FeaturePython — macro-defined, semantics opaque (R4)
  AssemblyType = Asm4EE
  AttachedBy = Origin
  AttachedTo = Art3Body_Art3Body#HoleAxis_15
  AttachmentOffset = pos=(0,0,0) rot=(1,0,0;3.14159rad)
  Placement = pos=(22.5,39,11) rot=(0,0,1;0rad)
  diameter = 4
  invert = false
  length = 6
  lengthCustom = 16
  matchOuter = false
  offset = 0
  thread = false
  type = 33
  expr: Placement = Art3Body_Art3Body.Placement * Art3Body#HoleAxis_15.Placement * AttachmentOffset
FEATURE [Part::FeaturePython] Screw019  label="M3x8-Screw017"  # WARN: FeaturePython — macro-defined, semantics opaque (R4)
  AssemblyType = Asm4EE
  AttachedBy = Origin
  AttachedTo = Art4MotorFix_Art4MotorFix#HoleAxis_5
  Placement = pos=(12.35,15.5,79.6) rot=(0,1,0;3.14159rad)
  diameter = 4
  invert = false
  length = 2
  lengthCustom = 8
  matchOuter = false
  offset = 0
  thread = false
  type = 33
  expr: Placement = Art4MotorFix_Art4MotorFix.Placement * Art4MotorFix#HoleAxis_5.Placement * AttachmentOffset
FEATURE [Part::FeaturePython] Screw020  label="M3x8-Screw018"  # WARN: FeaturePython — macro-defined, semantics opaque (R4)
  AssemblyType = Asm4EE
  AttachedBy = Origin
  AttachedTo = Art4MotorFix_Art4MotorFix#HoleAxis_6
  Placement = pos=(12.35,-15.5,79.6) rot=(0,1,0;3.14159rad)
  diameter = 4
  invert = false
  length = 2
  lengthCustom = 8
  matchOuter = false
  offset = 0
  thread = false
  type = 33
  expr: Placement = Art4MotorFix_Art4MotorFix.Placement * Art4MotorFix#HoleAxis_6.Placement * AttachmentOffset
FEATURE [Part::FeaturePython] Screw021  label="M3x8-Screw019"  # WARN: FeaturePython — macro-defined, semantics opaque (R4)
  AssemblyType = Asm4EE
  AttachedBy = Origin
  AttachedTo = Art4MotorFix_Art4MotorFix#HoleAxis_4
  Placement = pos=(43.35,15.5,79.6) rot=(0,1,0;3.14159rad)
  diameter = 4
  invert = false
  length = 2
  lengthCustom = 8
  matchOuter = false
  offset = 0
  thread = false
  type = 33
  expr: Placement = Art4MotorFix_Art4MotorFix.Placement * Art4MotorFix#HoleAxis_4.Placement * AttachmentOffset
FEATURE [Part::FeaturePython] Screw022  label="M3x8-Screw020"  # WARN: FeaturePython — macro-defined, semantics opaque (R4)
  AssemblyType = Asm4EE
  AttachedBy = Origin
  AttachedTo = Art4MotorFix_Art4MotorFix#HoleAxis_1
  Placement = pos=(43.35,-15.5,79.6) rot=(0,1,0;3.14159rad)
  diameter = 4
  invert = false
  length = 2
  lengthCustom = 8
  matchOuter = false
  offset = 0
  thread = false
  type = 33
  expr: Placement = Art4MotorFix_Art4MotorFix.Placement * Art4MotorFix#HoleAxis_1.Placement * AttachmentOffset
FEATURE [Part::FeaturePython] Screw023  label="M3x6-Screw"  # WARN: FeaturePython — macro-defined, semantics opaque (R4)
  AssemblyType = Asm4EE
  AttachedBy = Origin
  AttachedTo = Art3Body_Art3Body#HoleAxis_6
  AttachmentOffset = pos=(0,0,0) rot=(1,0,0;3.14159rad)
  Placement = pos=(51,4.5,77.6) rot=(0.57735,-0.57735,0.57735;4.18879rad)
  diameter = 4
  invert = false
  length = 1
  lengthCustom = 6
  matchOuter = false
  offset = 0
  thread = false
  type = 33
  expr: Placement = Art3Body_Art3Body.Placement * Art3Body#HoleAxis_6.Placement * AttachmentOffset
FEATURE [Part::FeaturePython] Screw024  label="M3x6-Screw001"  # WARN: FeaturePython — macro-defined, semantics opaque (R4)
  AssemblyType = Asm4EE
  AttachedBy = Origin
  AttachedTo = Art3Body_Art3Body#HoleAxis_5
  AttachmentOffset = pos=(0,0,0) rot=(1,0,0;3.14159rad)
  Placement = pos=(51,-4.5,77.6) rot=(0.57735,-0.57735,0.57735;4.18879rad)
  diameter = 4
  invert = false
  length = 1
  lengthCustom = 6
  matchOuter = false
  offset = 0
  thread = false
  type = 33
  expr: Placement = Art3Body_Art3Body.Placement * Art3Body#HoleAxis_5.Placement * AttachmentOffset
FEATURE [Part::FeaturePython] Screw025  label="M3x8-Screw021"  # WARN: FeaturePython — macro-defined, semantics opaque (R4)
  AssemblyType = Asm4EE
  AttachedBy = Origin
  AttachedTo = Art4MotorGear_Art4MotorGear#HoleAxis_1
  AttachmentOffset = pos=(0,0,0) rot=(1,0,0;3.14159rad)
  Placement = pos=(36.85,2.7e-14,71.1) rot=(0.57735,0.57735,0.57735;2.0944rad)
  diameter = 4
  invert = false
  length = 2
  lengthCustom = 8
  matchOuter = false
  offset = 0
  thread = false
  type = 33
  expr: Placement = Art4MotorGear_Art4MotorGear.Placement * Art4MotorGear#HoleAxis_1.Placement * AttachmentOffset
FEATURE [App::DocumentObjectGroup] Group003  label="Fasteners"
  Group = -> [Nut001,Nut002,Nut003,Nut,Nut004,Nut005,Nut006,Nut007,Nut008,Nut009,Nut010,Nut012,Nut011,Nut013,Nut014,Nut015,Nut016,Nut017,Nut018,Nut019,Nut020,Nut021,Screw001,Screw002,Screw003,Screw004,Screw006,Screw005,Screw008,Screw007,Screw009,Screw010,Screw011,Screw012,Screw013,Screw014,Screw015,Screw016,Screw017,Screw018,Screw019,Screw020,Screw021,Screw022,Screw023,Screw024,Screw,Screw025]
FEATURE [PartDesign::CoordinateSystem] LCS_Art2Fix
  AttacherType = Attacher::AttachEngine3D
  MapMode = 0
  Placement = pos=(0,0,81.5) rot=(0,0,1;0rad)
FEATURE [PartDesign::CoordinateSystem] LCS_Art4Fix
  AttacherType = Attacher::AttachEngine3D
  MapMode = 0
  Placement = pos=(0,0,-1) rot=(0,0,1;0rad)
FEATURE [App::Part] Model
  Configuration = 0
  Group = -> [LCS_Origin,Constraints,Variables,Art3Body_Art3Body,Art23Optodisk_Art23Optodisk,Art3Pulley_Art3Pulley,Art4MotorFix_Art4MotorFix,Stepper_Nema17x34001,Art4MotorGear_Art4MotorGear,Fan_40x40001,Bearing_625ZZ001,Bearing_625ZZ002,CommonBearingFixThrough_CommonBearingFixThrough,CommonBearingFixThrough_CommonBearingFixThrough001,OpticSensor,Art4BearingRing_Art4BearingRing,BearingBalls,LCS_Art2Fix,LCS_Art4F]
  Origin = -> Origin
  Type = Assembly4 Model
